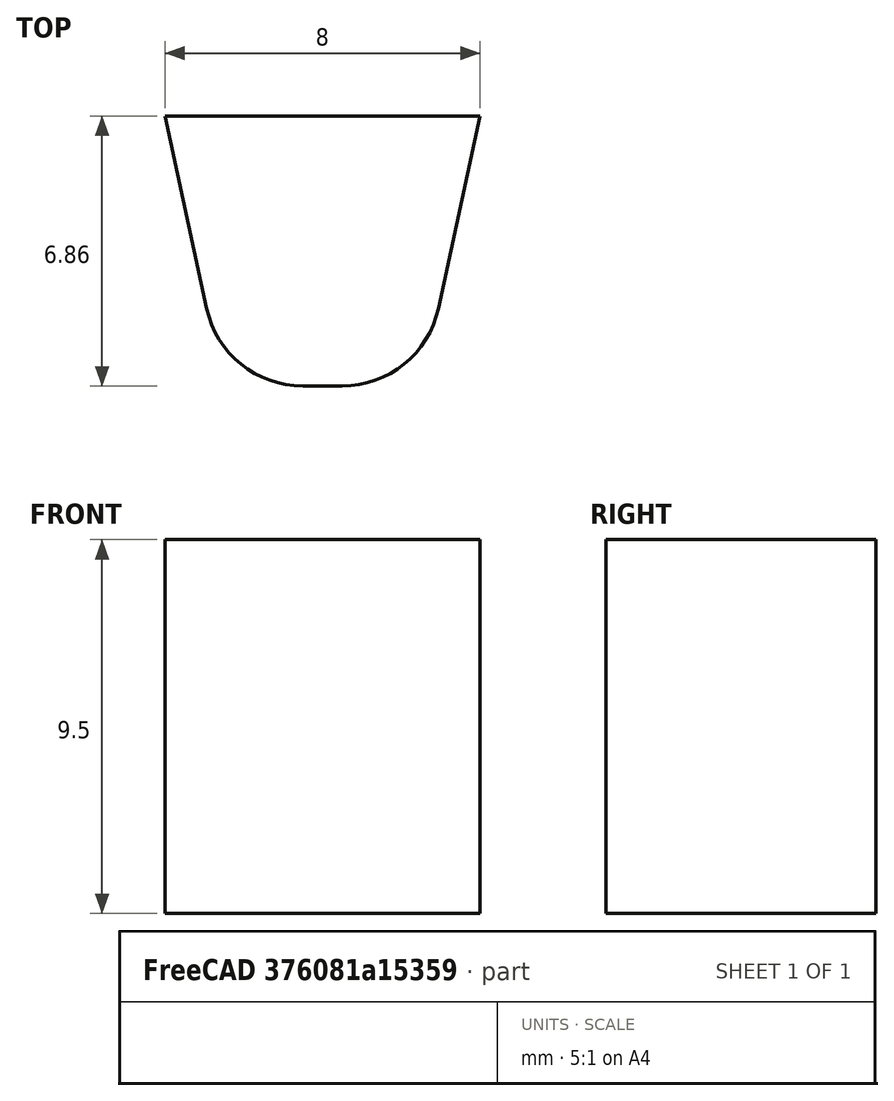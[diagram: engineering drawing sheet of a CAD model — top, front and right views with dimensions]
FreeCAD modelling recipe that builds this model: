
FCSTD DOCUMENT  (FreeCAD 0.21R33668 +26 (Git))
Label: HeatSetInsertHolder
License: All rights reserved
LicenseURL: http://en.wikipedia.org/wiki/All_rights_reserved
objects: Sketcher::SketchObject×1, PartDesign::Pad×1, PartDesign::Body×1, Part::Refine×1
note: 5 computed .brp shape members not serialized (recipe doc carries the construction recipe); baked Part::Feature solids carry a one-line shape summary decoded from their .brp

FEATURE [Sketcher::SketchObject] Sketch018
  AttachmentOffset = pos=(0,0,-1) rot=(0,0,1;0rad)
  FullyConstrained = true
  MapMode = 5
  Placement = pos=(0,0,-1) rot=(0,0,1;0rad)
  Support = -> [XY_Plane009]
  sketch-geometry (9):
    g0: LineSegment StartX=-4 StartY=3.8589 StartZ=0 EndX=4 EndY=3.8589 EndZ=0
    g1: LineSegment StartX=4 StartY=3.8589 StartZ=0 EndX=2.94356 EndY=-1.02822 EndZ=0
    g2: LineSegment StartX=0.5 StartY=-3 StartZ=0 EndX=-0.5 EndY=-3 EndZ=0
    g3: LineSegment StartX=-2.94356 StartY=-1.02822 StartZ=0 EndX=-4 EndY=3.8589 EndZ=0
    g4: ArcOfCircle CenterX=-0.5 CenterY=-0.5 CenterZ=0 NormalX=0 NormalY=0 NormalZ=1 AngleXU=0 Radius=2.5 StartAngle=3.35449 EndAngle=4.71239
    g5: ArcOfCircle CenterX=0.5 CenterY=-0.5 CenterZ=0 NormalX=0 NormalY=0 NormalZ=1 AngleXU=0 Radius=2.5 StartAngle=4.71239 EndAngle=6.07029
    g6: GeomPoint X=0 Y=0 Z=0
    g7: LineSegment StartX=-0.5 StartY=-0.5 StartZ=0 EndX=0 EndY=0 EndZ=0
    g8: LineSegment StartX=0 StartY=0 StartZ=0 EndX=0.5 EndY=-0.5 EndZ=0
  constraints (21):
    c: Coincident(g0,g1)
    c: Coincident(g3,g0)
    c: Horizontal(g0)
    c: Horizontal(g2)
    c: Tangent(g3,g4) = 1.5708
    c: Tangent(g2,g4) = 1.5708
    c: Tangent(g2,g5) = 1.5708
    c: Tangent(g1,g5) = 1.5708
    c: Equal(g4,g5)
    c: Equal(g1,g3)
    c: Radius(g4) = 2.5
    c: DistanceX(g2,g2) = 1
    c: DistanceX(g0,g0) = 8
    c: Distance(g1) = 5
    c: Coincident(g7,g4)
    c: Coincident(g7,g6)
    c: Coincident(g8,g7)
    c: Coincident(g8,g5)
    c: Equal(g8,g7)
    c: DistanceY(g5,g7) = 0.5
    c: Coincident(g6,g-1)
FEATURE [PartDesign::Pad] Pad009
  Direction = (0,0,1)
  Length = 9.5
  Length2 = 10
  Profile = -> Sketch018
  ReferenceAxis = -> Sketch018 [N_Axis]
  Reversed = true
  Type = 0
  expr: Length = 12 mm - 1.5 mm - 1 mm
FEATURE [PartDesign::Body] Body009  label="HeatsetHolder"
  Group = -> [Sketch018,Pad009]
  Origin = -> Origin009
  Tip = -> Pad009
FEATURE [Part::Refine] Body010  label="HeatsetHolderR"
  Source = -> Body009
